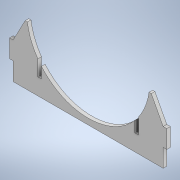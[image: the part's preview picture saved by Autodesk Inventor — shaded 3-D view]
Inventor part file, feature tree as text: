
AUTODESK INVENTOR PART (.ipt)
format: ipt  version: 2022 (Build 260153000, 153)  size: 187,904 bytes
history: native  units: mm
features: extrude x7, sketch x7, other x1
ambient origin geometry x8: Origin, YZ Plane, XZ Plane, XY Plane, X Axis, Y Axis, Z Axis, Center Point
bodies: Body1 (feature_tree)
feature tree (15):
  other  "Твердое тело1"
  extrude  "Выдавливание1"  Depth=332.0mm
  extrude  "Выдавливание2"  Depth=149.0mm
  extrude  "Выдавливание3"  Depth=166.0mm
  extrude  "Выдавливание4"  Depth=74.5mm
  extrude  "Выдавливание5"  Depth=8.0mm TaperAngle=0.0deg
  extrude  "Выдавливание6"  Depth=272.0mm
  extrude  "Выдавливание7"  TaperAngle=0.0deg  [1 undecoded]
  sketch  "Эскиз1"
  sketch  "Эскиз2"
  sketch  "Эскиз3"
  sketch  "Эскиз4"
  sketch  "Эскиз5"
  sketch  "Эскиз6"
  sketch  "Эскиз7"
note: 1 required parameter value undecoded (feature->parameter linkage not recoverable at this tier; creation-order binding heuristic only, values carry confidence <= 0.55)
